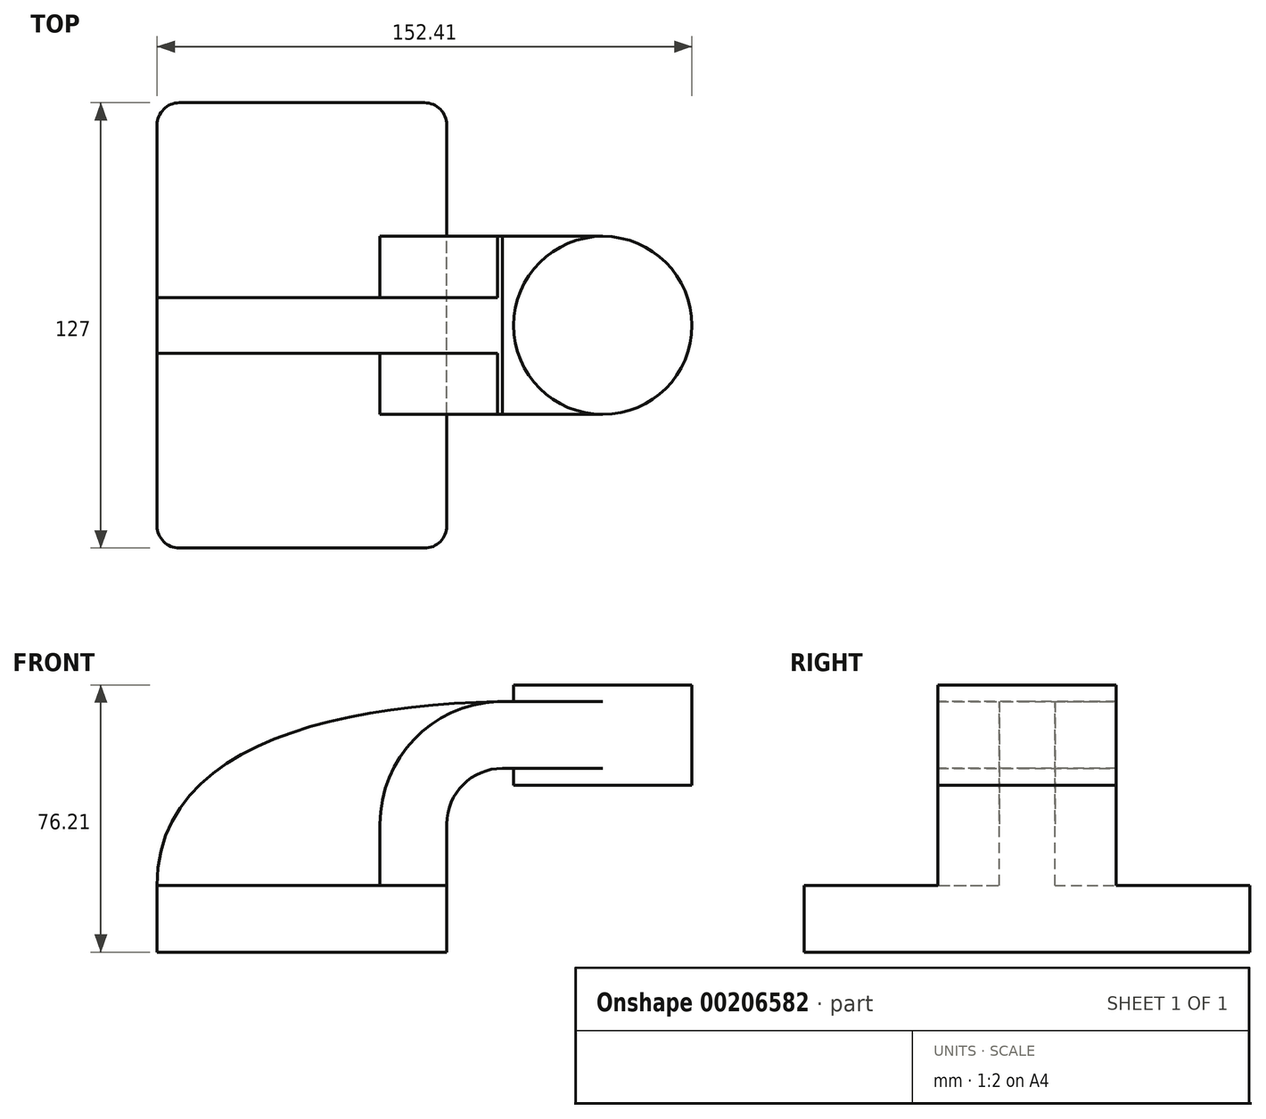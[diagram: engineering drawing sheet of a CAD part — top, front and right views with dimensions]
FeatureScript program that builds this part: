
annotation { "Feature Type Name" : "Feature", "Feature Type Description" : "" }
export const myFeature = defineFeature(function(context is Context, id is Id, definition is map)
    precondition{}
    {
        {
            var Q0;
            Q0=qCreatedBy(makeId("Front.planeOp"),FACE);
            var sketch = newSketch(context, id + "F0", { "sketchPlane" : qUnion([Q0])});
            skLineSegment(sketch, "E0.bottom", {"start": v(-41.28, 9.53) * mm, "end": v(41.28, 9.53) * mm});
            skLineSegment(sketch, "E0.top", {"start": v(-41.28, -9.52) * mm, "end": v(41.28, -9.52) * mm});
            skLineSegment(sketch, "E0.left", {"start": v(-41.28, 9.52) * mm, "end": v(-41.28, -9.53) * mm});
            skLineSegment(sketch, "E0.right", {"start": v(41.28, 9.53) * mm, "end": v(41.28, -9.52) * mm});
            skPoint(sketch, "E0.middle", {"position": v(0, 0) * mm});
            skLineSegment(sketch, "E1.bottom", {"start": v(60.33, 38.1) * mm, "end": v(111.12, 38.1) * mm});
            skLineSegment(sketch, "E1.top", {"start": v(60.33, 66.67) * mm, "end": v(111.12, 66.67) * mm});
            skLineSegment(sketch, "E1.left", {"start": v(60.33, 38.1) * mm, "end": v(60.33, 66.68) * mm});
            skLineSegment(sketch, "E1.right", {"start": v(111.13, 38.1) * mm, "end": v(111.13, 66.68) * mm});
            skPoint(sketch, "E1.middle", {"position": v(85.72, 52.39) * mm});
            skLineSegment(sketch, "E2", {"start": v(41.28, 9.53) * mm, "end": v(41.28, 27) * mm});
            skArc(sketch, "E3", {"start": v(41.27, 27) * mm, "mid": v(45.92, 38.23) * mm, "end": v(57.15, 42.88) * mm});
            skLineSegment(sketch, "E4", {"start": v(57.15, 42.88) * mm, "end": v(85.72, 42.88) * mm});
            skPoint(sketch, "E4.endSnap0", {"position": v(85.72, 38.1) * mm});
            skLineSegment(sketch, "E5.0", {"start": v(57.15, 61.93) * mm, "end": v(85.72, 61.93) * mm});
            skArc(sketch, "E5.1", {"start": v(22.22, 27) * mm, "mid": v(32.45, 51.7) * mm, "end": v(57.15, 61.93) * mm});
            skLineSegment(sketch, "E5.2", {"start": v(22.23, 9.52) * mm, "end": v(22.23, 27) * mm});
            skLineSegment(sketch, "E6", {"start": v(85.72, 38.1) * mm, "end": v(85.72, 66.67) * mm});
            skFitSpline(sketch, "E7", {"points": [v(-41.28, 9.52) * mm, v(57.15, 61.93) * mm], "startDerivative": vector(-0.52, 120.46) * mm, "endDerivative": vector(141.16, 2.66) * mm});
            skSolve(sketch);
        }
        {
            var Q0;
            Q0=makeQuery(id+"F0.imprint","IMPRINT",FACE,{"disambiguationData":[TD([[makeQuery(id+"F0.imprint","IMPRINT",EDGE,{"derivedFrom":sQuery(id+"F0.wireOp",EDGE,"E0.bottom")}),-1.0]])]});
            extrude(context, id + "F1", {"entities" : qUnion([Q0]), "endBound" : BoundingType.SYMMETRIC, "depth" : 127 * mm});
        }
        {
            var Q0;
            {var subQ1=sQuery(id+"F0.wireOp",EDGE,"E2");Q0=makeQuery(id+"F0.imprint","IMPRINT",FACE,{"disambiguationData":[TD([[makeQuery(id+"F0.imprint","IMPRINT",EDGE,{"derivedFrom":subQ1}),1.0]])]});}
            var Q1;
            {var subQ0=sQuery(id+"F0.wireOp",EDGE,"E4");var subQ1=sQuery(id+"F0.wireOp",EDGE,"E1.left");var subQ2=makeQuery(id+"F0.imprint","INTERSECT",VERTEX,{"derivedFrom":[subQ1,subQ0]});Q1=makeQuery(id+"F0.imprint","IMPRINT",FACE,{"disambiguationData":[TD([[makeQuery(id+"F0.imprint","IMPRINT",EDGE,{"disambiguationData":[TD([[subQ2,-1.0]])],"derivedFrom":subQ1}),-1.0]])]});}
            extrude(context, id + "F2", {"entities" : qUnion([Q0, Q1]), "operationType" : NewBodyOperationType.ADD, "endBound" : BoundingType.SYMMETRIC, "depth" : 50.8 * mm});
        }
        {
            var Q0;
            {var subQ3=sQuery(id+"F0.wireOp",EDGE,"E5.2");Q0=makeQuery(id+"F0.imprint","IMPRINT",FACE,{"disambiguationData":[TD([[makeQuery(id+"F0.imprint","IMPRINT",EDGE,{"derivedFrom":subQ3}),1.0]])]});}
            extrude(context, id + "F3", {"entities" : qUnion([Q0]), "operationType" : NewBodyOperationType.ADD, "endBound" : BoundingType.SYMMETRIC, "depth" : 15.88 * mm});
        }
        {
            var Q0;
            {var subQ0=sQuery(id+"F0.wireOp",EDGE,"E1.right");Q0=makeQuery(id+"F0.imprint","IMPRINT",FACE,{"disambiguationData":[TD([[makeQuery(id+"F0.imprint","IMPRINT",EDGE,{"derivedFrom":subQ0}),1.0]])]});}
            var Q1;
            Q1=sQuery(id+"F0.wireOp",EDGE,"E6");
            revolve(context, id + "F4", {"operationType" : NewBodyOperationType.ADD, "entities" : qUnion([Q0]), "axis" : qUnion([Q1]), "revolveType" : RevolveType.FULL});
        }
        {
            var Q0;
            Q0=makeQuery(id+"F1.opExtrude","CAP_EDGE",EDGE,{"disambiguationData":[OSD([sQuery(id+"F0.wireOp",EDGE,"E0.right")])],"isStart":true});
            var Q1;
            Q1=makeQuery(id+"F1.opExtrude","CAP_EDGE",EDGE,{"disambiguationData":[OSD([sQuery(id+"F0.wireOp",EDGE,"E0.left")])],"isStart":true});
            var Q2;
            Q2=makeQuery(id+"F1.opExtrude","CAP_EDGE",EDGE,{"disambiguationData":[OSD([sQuery(id+"F0.wireOp",EDGE,"E0.left")])],"isStart":false});
            var Q3;
            Q3=makeQuery(id+"F1.opExtrude","CAP_EDGE",EDGE,{"disambiguationData":[OSD([sQuery(id+"F0.wireOp",EDGE,"E0.right")])],"isStart":false});
            fillet(context, id + "F5", {"entities" : qUnion([Q0, Q1, Q2, Q3]), "radius" : 6.35 * mm, "tangentPropagation" : true, "allowEdgeOverflow" : false});
        }
    });
